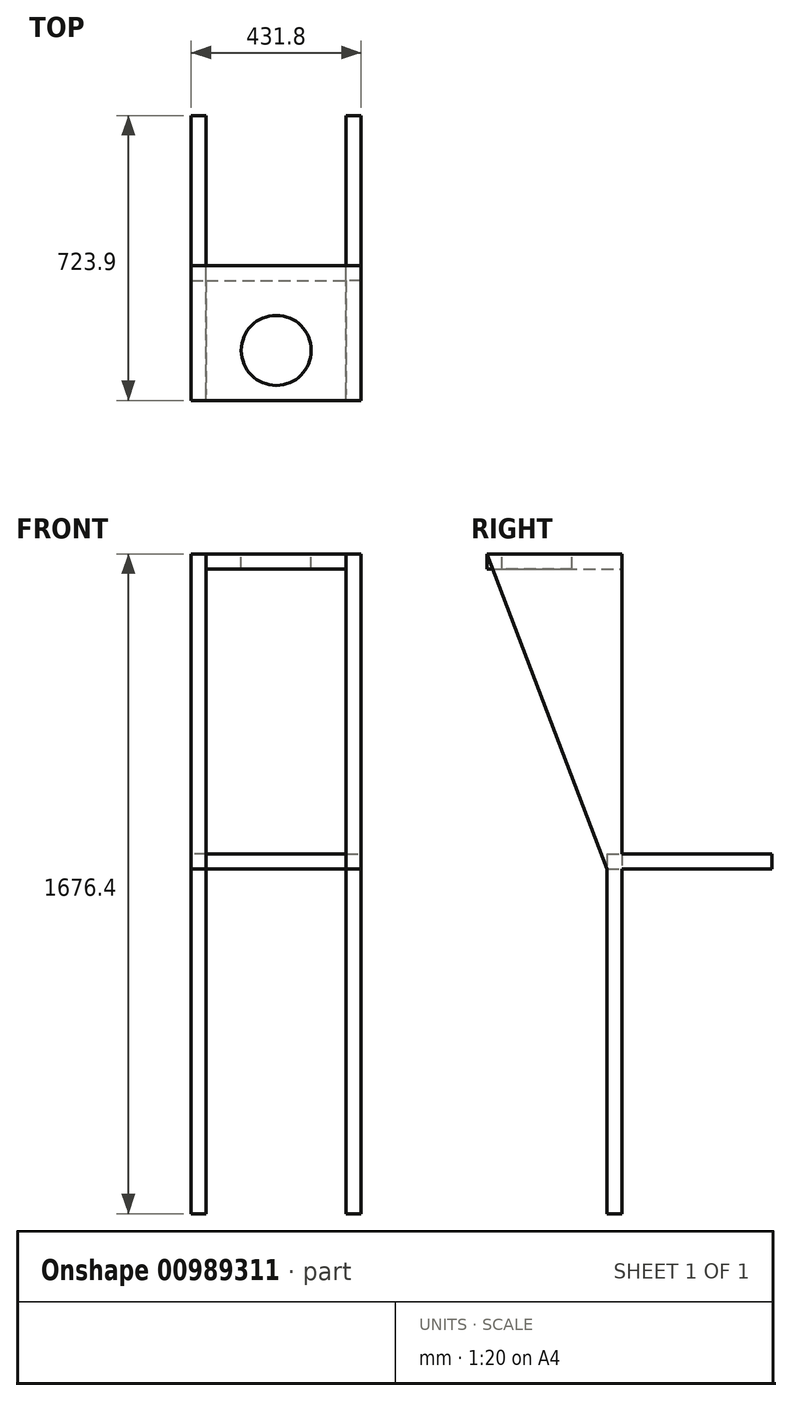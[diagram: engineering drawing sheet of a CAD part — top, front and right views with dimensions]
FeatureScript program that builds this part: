
annotation { "Feature Type Name" : "Feature", "Feature Type Description" : "" }
export const myFeature = defineFeature(function(context is Context, id is Id, definition is map)
    precondition{}
    {
        {
            var Q0;
            Q0=qCreatedBy(makeId("Front.planeOp"),FACE);
            var sketch = newSketch(context, id + "F0", { "sketchPlane" : qUnion([Q0])});
            skLineSegment(sketch, "E0.bottom", {"start": v(-85.37, 0) * mm, "end": v(-47.27, 0) * mm});
            skLineSegment(sketch, "E0.top", {"start": v(-85.37, -1676.4) * mm, "end": v(-47.27, -1676.4) * mm});
            skLineSegment(sketch, "E0.left", {"start": v(-85.37, 0) * mm, "end": v(-85.37, -1676.4) * mm});
            skLineSegment(sketch, "E0.right", {"start": v(-47.27, 0) * mm, "end": v(-47.27, -1676.4) * mm});
            skLineSegment(sketch, "E1.bottom", {"start": v(-47.27, 0) * mm, "end": v(308.33, 0) * mm});
            skLineSegment(sketch, "E1.top", {"start": v(-47.27, -38.1) * mm, "end": v(308.33, -38.1) * mm});
            skLineSegment(sketch, "E1.left", {"start": v(-47.27, 0) * mm, "end": v(-47.27, -38.1) * mm});
            skLineSegment(sketch, "E1.right", {"start": v(308.33, 0) * mm, "end": v(308.33, -38.1) * mm});
            skLineSegment(sketch, "E2.bottom", {"start": v(308.33, 0) * mm, "end": v(346.43, 0) * mm});
            skLineSegment(sketch, "E2.top", {"start": v(308.33, -1676.4) * mm, "end": v(346.43, -1676.4) * mm});
            skLineSegment(sketch, "E2.left", {"start": v(308.33, 0) * mm, "end": v(308.33, -1676.4) * mm});
            skLineSegment(sketch, "E2.right", {"start": v(346.43, 0) * mm, "end": v(346.43, -1676.4) * mm});
            skLineSegment(sketch, "E3.bottom", {"start": v(-47.27, -762) * mm, "end": v(308.33, -762) * mm});
            skLineSegment(sketch, "E3.top", {"start": v(-47.27, -800.1) * mm, "end": v(308.33, -800.1) * mm});
            skLineSegment(sketch, "E3.left", {"start": v(-47.27, -762) * mm, "end": v(-47.27, -800.1) * mm});
            skLineSegment(sketch, "E3.right", {"start": v(308.33, -762) * mm, "end": v(308.33, -800.1) * mm});
            skSolve(sketch);
        }
        {
            var Q0;
            Q0 = qSketchRegion(id + "F0", true);
            extrude(context, id + "F1", {"entities" : qUnion([Q0]), "depth" : 38.1 * mm, "offsetDistance" : 25.4 * mm});
        }
        {
            var Q0;
            Q0=makeQuery(id+"F1.opExtrude","CAP_FACE",FACE,{"disambiguationData":[OSD([sQuery(id+"F0.wireOp",EDGE,"E0.bottom"),sQuery(id+"F0.wireOp",EDGE,"E0.top"),sQuery(id+"F0.wireOp",EDGE,"E0.left"),sQuery(id+"F0.wireOp",EDGE,"E0.right"),sQuery(id+"F0.wireOp",EDGE,"E1.bottom"),sQuery(id+"F0.wireOp",EDGE,"E1.top"),sQuery(id+"F0.wireOp",EDGE,"E2.bottom"),sQuery(id+"F0.wireOp",EDGE,"E2.top"),sQuery(id+"F0.wireOp",EDGE,"E2.left"),sQuery(id+"F0.wireOp",EDGE,"E2.right"),sQuery(id+"F0.wireOp",EDGE,"E3.bottom"),sQuery(id+"F0.wireOp",EDGE,"E3.top")])],"isStart":true});
            var sketch = newSketch(context, id + "F2", { "sketchPlane" : qUnion([Q0])});
            skLineSegment(sketch, "E4.bottom", {"start": v(-308.33, -762) * mm, "end": v(-346.43, -762) * mm});
            skLineSegment(sketch, "E4.top", {"start": v(-308.33, -800.1) * mm, "end": v(-346.43, -800.1) * mm});
            skLineSegment(sketch, "E4.left", {"start": v(-308.33, -762) * mm, "end": v(-308.33, -800.1) * mm});
            skLineSegment(sketch, "E4.right", {"start": v(-346.43, -762) * mm, "end": v(-346.43, -800.1) * mm});
            skLineSegment(sketch, "E5.bottom", {"start": v(47.27, -762) * mm, "end": v(85.37, -762) * mm});
            skLineSegment(sketch, "E5.top", {"start": v(47.27, -800.1) * mm, "end": v(85.37, -800.1) * mm});
            skLineSegment(sketch, "E5.left", {"start": v(47.27, -762) * mm, "end": v(47.27, -800.1) * mm});
            skLineSegment(sketch, "E5.right", {"start": v(85.37, -762) * mm, "end": v(85.37, -800.1) * mm});
            skSolve(sketch);
        }
        {
            var Q0;
            Q0 = qSketchRegion(id + "F2", true);
            extrude(context, id + "F3", {"entities" : qUnion([Q0]), "operationType" : NewBodyOperationType.ADD, "depth" : 381 * mm, "offsetDistance" : 25.4 * mm});
        }
        {
            var Q0;
            Q0=makeQuery(id+"F1.opExtrude","CAP_FACE",FACE,{"disambiguationData":[OSD([sQuery(id+"F0.wireOp",EDGE,"E0.bottom"),sQuery(id+"F0.wireOp",EDGE,"E0.top"),sQuery(id+"F0.wireOp",EDGE,"E0.left"),sQuery(id+"F0.wireOp",EDGE,"E0.right"),sQuery(id+"F0.wireOp",EDGE,"E1.bottom"),sQuery(id+"F0.wireOp",EDGE,"E1.top"),sQuery(id+"F0.wireOp",EDGE,"E2.bottom"),sQuery(id+"F0.wireOp",EDGE,"E2.top"),sQuery(id+"F0.wireOp",EDGE,"E2.left"),sQuery(id+"F0.wireOp",EDGE,"E2.right"),sQuery(id+"F0.wireOp",EDGE,"E3.bottom"),sQuery(id+"F0.wireOp",EDGE,"E3.top")])],"isStart":false});
            var sketch = newSketch(context, id + "F4", { "sketchPlane" : qUnion([Q0])});
            skLineSegment(sketch, "E6.bottom", {"start": v(-85.37, 0) * mm, "end": v(-47.27, 0) * mm});
            skLineSegment(sketch, "E6.top", {"start": v(-85.37, -800.1) * mm, "end": v(-47.27, -800.1) * mm});
            skLineSegment(sketch, "E6.left", {"start": v(-85.37, 0) * mm, "end": v(-85.37, -800.1) * mm});
            skLineSegment(sketch, "E6.right", {"start": v(-47.27, 0) * mm, "end": v(-47.27, -800.1) * mm});
            skLineSegment(sketch, "E7.bottom", {"start": v(346.43, 0) * mm, "end": v(308.33, 0) * mm});
            skLineSegment(sketch, "E7.top", {"start": v(346.43, -800.1) * mm, "end": v(308.33, -800.1) * mm});
            skLineSegment(sketch, "E7.left", {"start": v(346.43, 0) * mm, "end": v(346.43, -800.1) * mm});
            skLineSegment(sketch, "E7.right", {"start": v(308.33, 0) * mm, "end": v(308.33, -800.1) * mm});
            skLineSegment(sketch, "E8.bottom", {"start": v(-47.27, 0) * mm, "end": v(308.33, 0) * mm});
            skLineSegment(sketch, "E8.top", {"start": v(-47.27, -38.1) * mm, "end": v(308.33, -38.1) * mm});
            skLineSegment(sketch, "E8.left", {"start": v(-47.27, 0) * mm, "end": v(-47.27, -38.1) * mm});
            skLineSegment(sketch, "E8.right", {"start": v(308.33, 0) * mm, "end": v(308.33, -38.1) * mm});
            skSolve(sketch);
        }
        {
            var Q0;
            Q0 = qSketchRegion(id + "F4", true);
            extrude(context, id + "F5", {"entities" : qUnion([Q0]), "operationType" : NewBodyOperationType.ADD, "depth" : 304.8 * mm, "offsetDistance" : 25.4 * mm});
        }
        {
            var Q0;
            Q0=makeQuery(id+"F5.boolean.opBoolean","MERGE",FACE,{"derivedFrom":[makeQuery(id+"F3.boolean.opBoolean","MERGE",FACE,{"derivedFrom":[makeQuery(id+"F1.opExtrude","SWEPT_FACE",FACE,{"disambiguationData":[OSD([sQuery(id+"F0.wireOp",EDGE,"E0.left")])]}),makeQuery(id+"F3.opExtrude","SWEPT_FACE",FACE,{"disambiguationData":[OSD([sQuery(id+"F2.wireOp",EDGE,"E5.right")])]})]}),makeQuery(id+"F5.opExtrude","SWEPT_FACE",FACE,{"disambiguationData":[OSD([sQuery(id+"F4.wireOp",EDGE,"E6.left")])]})]});
            var sketch = newSketch(context, id + "F6", { "sketchPlane" : qUnion([Q0])});
            skLineSegment(sketch, "E9", {"start": v(38.1, -800.1) * mm, "end": v(342.9, 0) * mm});
            skSolve(sketch);
        }
        {
            var Q0;
            Q0 = qSketchRegion(id + "F6", true);
            var Q1;
            Q1=makeQuery(id+"F6.imprint","IMPRINT",FACE,{"disambiguationData":[TD([[makeQuery(id+"F6.imprint","IMPRINT",EDGE,{"derivedFrom":sQuery(id+"F6.wireOp",EDGE,"E9")}),-1.0]])]});
            extrude(context, id + "F7", {"entities" : qUnion([Q0, Q1]), "operationType" : NewBodyOperationType.REMOVE, "oppositeDirection" : true, "depth" : 38.1 * mm, "offsetDistance" : 25.4 * mm});
        }
        {
            var Q0;
            Q0=makeQuery(id+"F5.boolean.opBoolean","MERGE",FACE,{"derivedFrom":[makeQuery(id+"F3.boolean.opBoolean","MERGE",FACE,{"derivedFrom":[makeQuery(id+"F1.opExtrude","SWEPT_FACE",FACE,{"disambiguationData":[OSD([sQuery(id+"F0.wireOp",EDGE,"E2.right")])]}),makeQuery(id+"F3.opExtrude","SWEPT_FACE",FACE,{"disambiguationData":[OSD([sQuery(id+"F2.wireOp",EDGE,"E4.right")])]})]}),makeQuery(id+"F5.opExtrude","SWEPT_FACE",FACE,{"disambiguationData":[OSD([sQuery(id+"F4.wireOp",EDGE,"E7.left")])]})]});
            var sketch = newSketch(context, id + "F8", { "sketchPlane" : qUnion([Q0])});
            skLineSegment(sketch, "E10", {"start": v(-38.1, -800.1) * mm, "end": v(-342.9, 0) * mm});
            skSolve(sketch);
        }
        {
            var Q0;
            Q0 = qSketchRegion(id + "F8", true);
            var Q1;
            Q1=makeQuery(id+"F8.imprint","IMPRINT",FACE,{"disambiguationData":[TD([[makeQuery(id+"F8.imprint","IMPRINT",EDGE,{"derivedFrom":sQuery(id+"F8.wireOp",EDGE,"E10")}),1.0]])]});
            extrude(context, id + "F9", {"entities" : qUnion([Q0, Q1]), "operationType" : NewBodyOperationType.REMOVE, "oppositeDirection" : true, "depth" : 38.1 * mm, "offsetDistance" : 25.4 * mm});
        }
        {
            var Q0;
            Q0=makeQuery(id+"F5.boolean.opBoolean","MERGE",FACE,{"derivedFrom":[makeQuery(id+"F1.opExtrude","SWEPT_FACE",FACE,{"disambiguationData":[OSD([sQuery(id+"F0.wireOp",EDGE,"E0.bottom"),sQuery(id+"F0.wireOp",EDGE,"E1.bottom"),sQuery(id+"F0.wireOp",EDGE,"E2.bottom")])]}),makeQuery(id+"F5.opExtrude","SWEPT_FACE",FACE,{"disambiguationData":[OSD([sQuery(id+"F4.wireOp",EDGE,"E6.bottom"),sQuery(id+"F4.wireOp",EDGE,"E7.bottom"),sQuery(id+"F4.wireOp",EDGE,"E8.bottom")])]})]});
            var sketch = newSketch(context, id + "F10", { "sketchPlane" : qUnion([Q0])});
            skCircle(sketch, "E11", {"center": v(130.53, -215.9) * mm, "radius": 88.9 * mm});
            skSolve(sketch);
        }
        {
            var Q0;
            Q0 = qSketchRegion(id + "F10", true);
            extrude(context, id + "F11", {"entities" : qUnion([Q0]), "operationType" : NewBodyOperationType.REMOVE, "oppositeDirection" : true, "depth" : 38.1 * mm, "offsetDistance" : 25.4 * mm});
        }
    });
